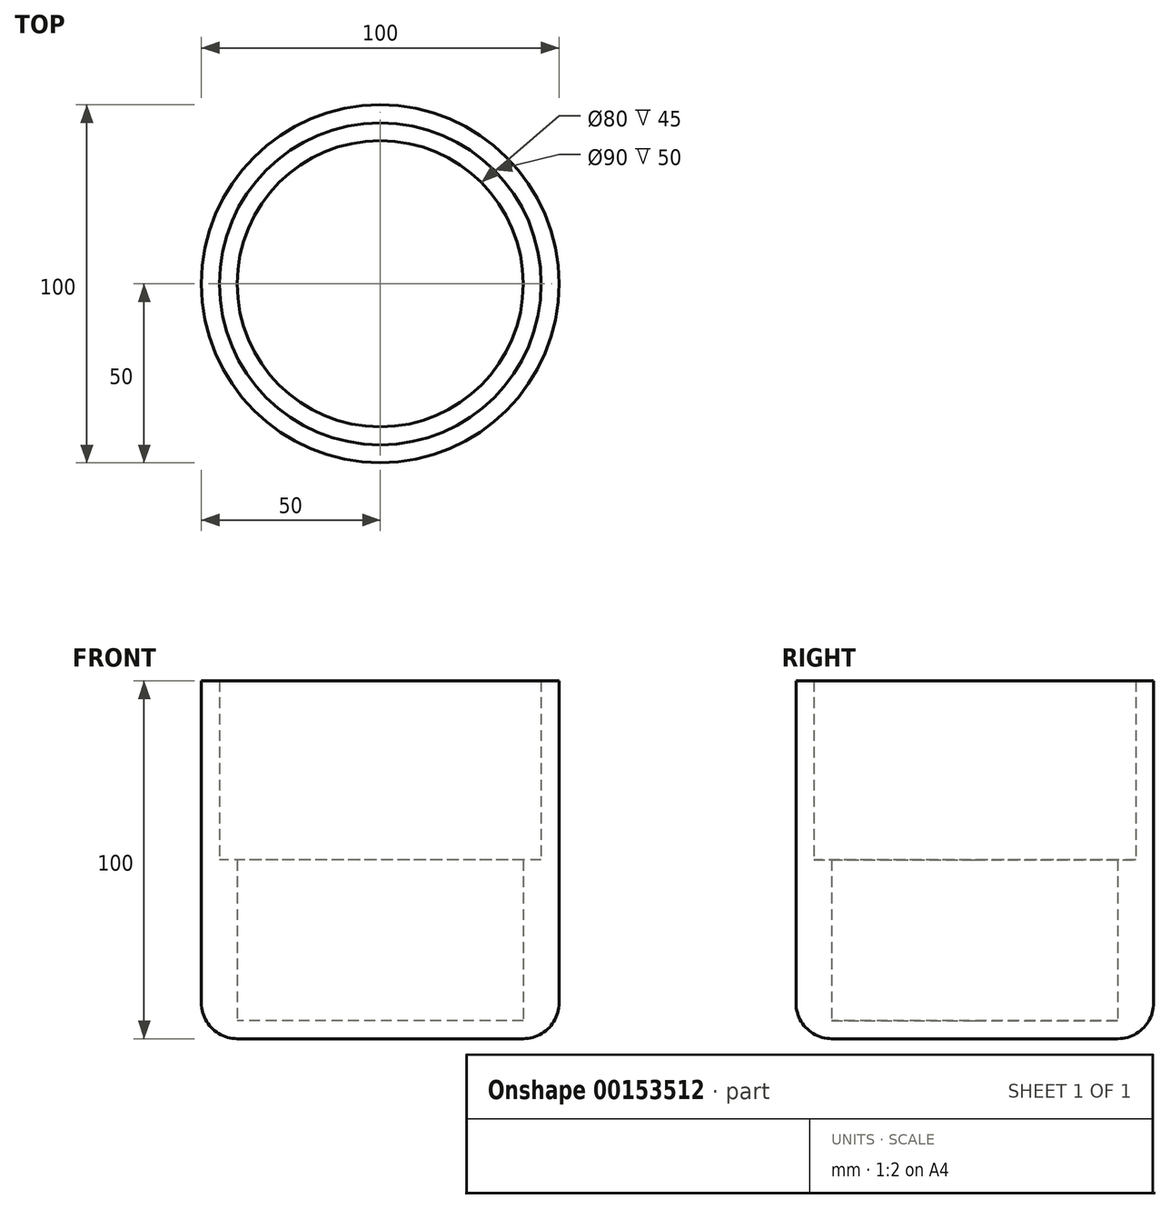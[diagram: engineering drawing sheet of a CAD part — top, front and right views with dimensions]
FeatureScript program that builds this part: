
annotation { "Feature Type Name" : "Feature", "Feature Type Description" : "" }
export const myFeature = defineFeature(function(context is Context, id is Id, definition is map)
    precondition{}
    {
        {
            var Q0;
            Q0=qCreatedBy(makeId("Top.planeOp"),FACE);
            var sketch = newSketch(context, id + "F0", { "sketchPlane" : qUnion([Q0])});
            skCircle(sketch, "E0", {"center": v(0, 0) * mm, "radius": 45 * mm});
            skCircle(sketch, "E1", {"center": v(0, 0) * mm, "radius": 50 * mm});
            skCircle(sketch, "E2", {"center": v(0, 0) * mm, "radius": 40 * mm});
            skSolve(sketch);
        }
        {
            var Q0;
            Q0=makeQuery(id+"F0.imprint","IMPRINT",FACE,{"disambiguationData":[TD([[makeQuery(id+"F0.imprint","IMPRINT",EDGE,{"derivedFrom":sQuery(id+"F0.wireOp",EDGE,"E0")}),1.0]])]});
            extrude(context, id + "F1", {"entities" : qUnion([Q0]), "depth" : 50 * mm});
        }
        {
            var Q0;
            Q0=makeQuery(id+"F0.imprint","IMPRINT",FACE,{"disambiguationData":[TD([[makeQuery(id+"F0.imprint","IMPRINT",EDGE,{"derivedFrom":sQuery(id+"F0.wireOp",EDGE,"E0")}),-1.0]])]});
            extrude(context, id + "F2", {"entities" : qUnion([Q0]), "operationType" : NewBodyOperationType.ADD, "depth" : 100 * mm});
        }
        {
            var Q0;
            Q0=makeQuery(id+"F0.imprint","IMPRINT",FACE,{"disambiguationData":[TD([[makeQuery(id+"F0.imprint","IMPRINT",EDGE,{"derivedFrom":sQuery(id+"F0.wireOp",EDGE,"E2")}),1.0]])]});
            var Q1;
            Q1=makeQuery(id+"F0.imprint","IMPRINT",FACE,{"disambiguationData":[TD([[makeQuery(id+"F0.imprint","IMPRINT",EDGE,{"derivedFrom":sQuery(id+"F0.wireOp",EDGE,"E0")}),1.0]])]});
            var Q2;
            Q2=makeQuery(id+"F0.imprint","IMPRINT",FACE,{"disambiguationData":[TD([[makeQuery(id+"F0.imprint","IMPRINT",EDGE,{"derivedFrom":sQuery(id+"F0.wireOp",EDGE,"E0")}),-1.0]])]});
            extrude(context, id + "F3", {"entities" : qUnion([Q0, Q1, Q2]), "operationType" : NewBodyOperationType.ADD, "depth" : 5 * mm});
        }
        {
            var Q0;
            Q0=makeQuery(id+"F2.opExtrude","CAP_EDGE",EDGE,{"disambiguationData":[OSD([sQuery(id+"F0.wireOp",EDGE,"E1")])],"isStart":true});
            fillet(context, id + "F4", {"entities" : qUnion([Q0]), "radius" : 10 * mm, "tangentPropagation" : true, "allowEdgeOverflow" : false});
        }
    });
